# Revit family: Seating_Inc-Jay_Nest-It_Guest-1
name_source: partatom
category: Furniture
revit_build: Autodesk Revit 2014 (Build: 20130308_1515(x64)
units: mm (PartAtom-declared; Revit-internal decimal feet)

## types (4) — shared parameters
Arm Finish = STI - Plastic Black
Arm V = No
Assembly Code = E2020200
Back Finish = STI - Plastic Black
Caster Finish = STI - Plastic Black
Depth = 22"
Front Finish = STI - Fabric Black
Glide Finish = STI - Plastic Black
Height = 33"
Keynote = 12500
Low Emitting Finish = Yes
Low Emitting Material = Yes
Manufacturer = Seating Inc
Plastic Finish = STI - Plastic Black
Salvage or Reuse = Yes
Seat Finish = STI - Leather
Type Comments = Quick Configuration
URL = www.seatinginc.com
zero-valued in all types: Percentage of Recycled Content

## per-type parameters (varying)
| type | Description | Frame Finish | Width |
| Q-3JN43B-A | Jay Nest-it Guest Guest Armless 20W x 22D x 33H (Black) | STI - Power Coat - Black | 20" |
| Q-3JN44B-B | Jay Nest-it Guest Guest with Arms  23.5W x 22D x 33H (Black) | STI - Power Coat - Black | 23 1/2" |
| Q-3JN43S-A | Jay Nest-it Guest Guest Armless 20W x 22D x 33H (Silver Metallic) | STI - Power Coat - Silver Metallic | 20" |
| Q-3JN44S-B | Jay Nest-it Guest Guest with Arms  23.5W x 22D x 33H (Silver Metallic) | STI - Power Coat - Silver Metallic | 23 1/2" |

note: column(s) folded — value = type name in every type: Model

## geometry (parser evidence)
native form markers: Sweep x4
no freeform markers — native parametric forms only
